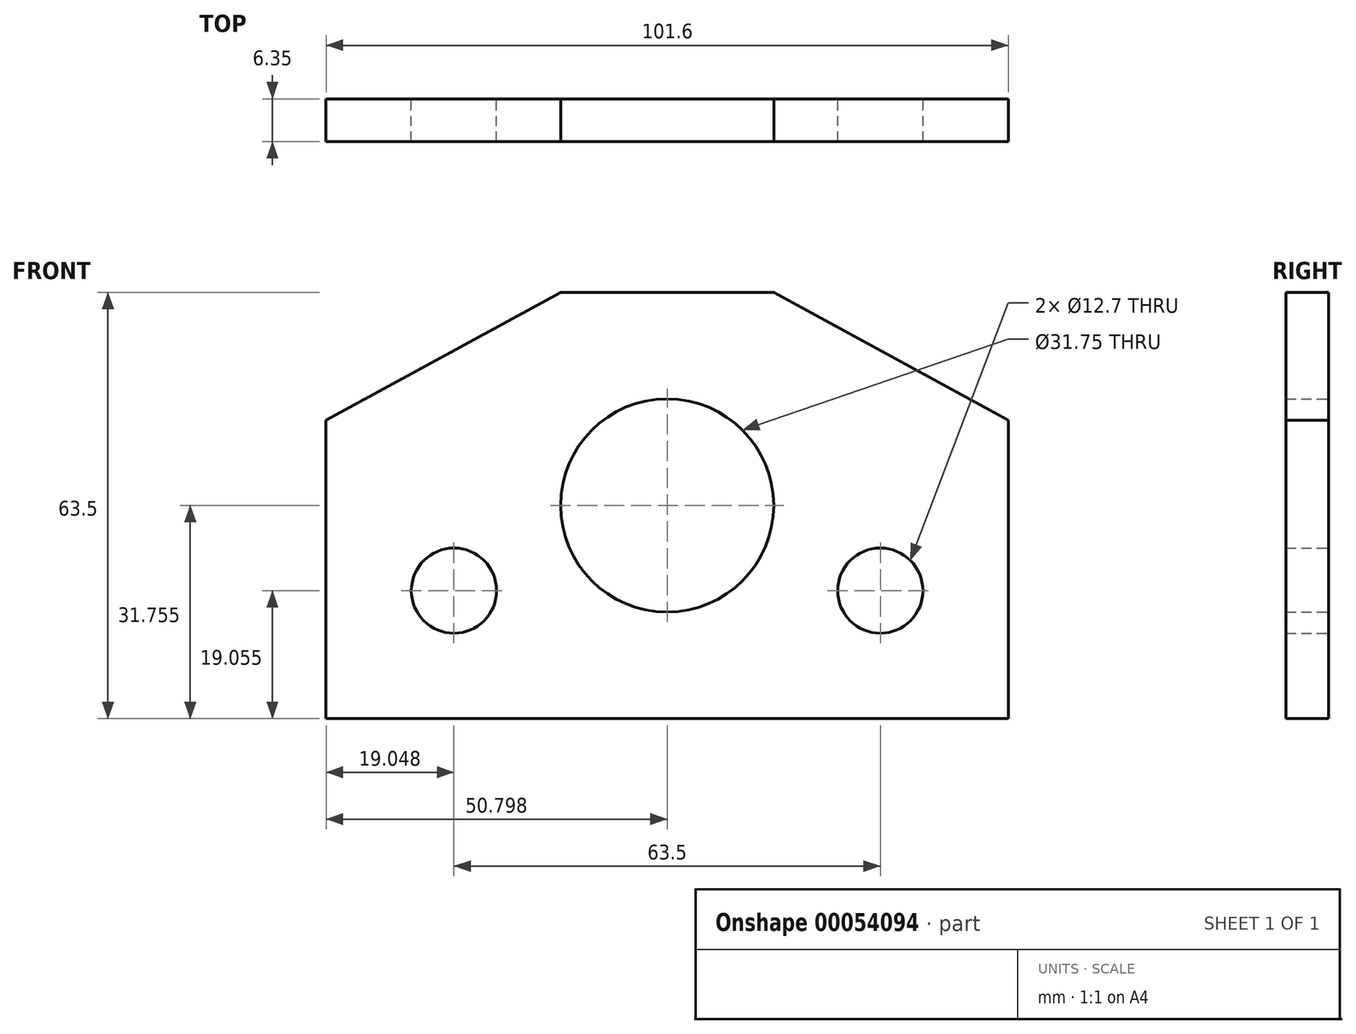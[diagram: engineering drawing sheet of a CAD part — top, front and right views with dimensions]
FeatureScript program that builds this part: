
annotation { "Feature Type Name" : "Feature", "Feature Type Description" : "" }
export const myFeature = defineFeature(function(context is Context, id is Id, definition is map)
    precondition{}
    {
        {
            var Q0;
            Q0=qCreatedBy(makeId("Front.planeOp"),FACE);
            var sketch = newSketch(context, id + "F0", { "sketchPlane" : qUnion([Q0])});
            skLineSegment(sketch, "E0", {"start": v(4.54, -1.16) * mm, "end": v(36.3, -1.16) * mm});
            skLineSegment(sketch, "E1", {"start": v(4.54, -1.16) * mm, "end": v(-30.38, -20.2) * mm});
            skLineSegment(sketch, "E2", {"start": v(-30.38, -64.66) * mm, "end": v(-30.38, -20.2) * mm});
            skLineSegment(sketch, "E3", {"start": v(71.22, -20.2) * mm, "end": v(71.22, -64.66) * mm});
            skLineSegment(sketch, "E4", {"start": v(-30.38, -64.66) * mm, "end": v(71.22, -64.66) * mm});
            skLineSegment(sketch, "E5", {"start": v(20.42, -64.66) * mm, "end": v(20.42, -1.16) * mm, "construction": true});
            skPoint(sketch, "E6", {"position": v(20.42, -1.16) * mm});
            skLineSegment(sketch, "E7", {"start": v(36.3, -1.16) * mm, "end": v(71.22, -20.2) * mm});
            skCircle(sketch, "E8", {"center": v(-11.33, -45.6) * mm, "radius": 6.35 * mm});
            skCircle(sketch, "E9", {"center": v(20.42, -32.9) * mm, "radius": 15.88 * mm});
            skCircle(sketch, "E10", {"center": v(52.17, -45.6) * mm, "radius": 6.35 * mm});
            skSolve(sketch);
        }
        {
            var Q0;
            Q0 = qSketchRegion(id + "F0", true);
            extrude(context, id + "F1", {"entities" : qUnion([Q0]), "depth" : 6.35 * mm});
        }
    });
